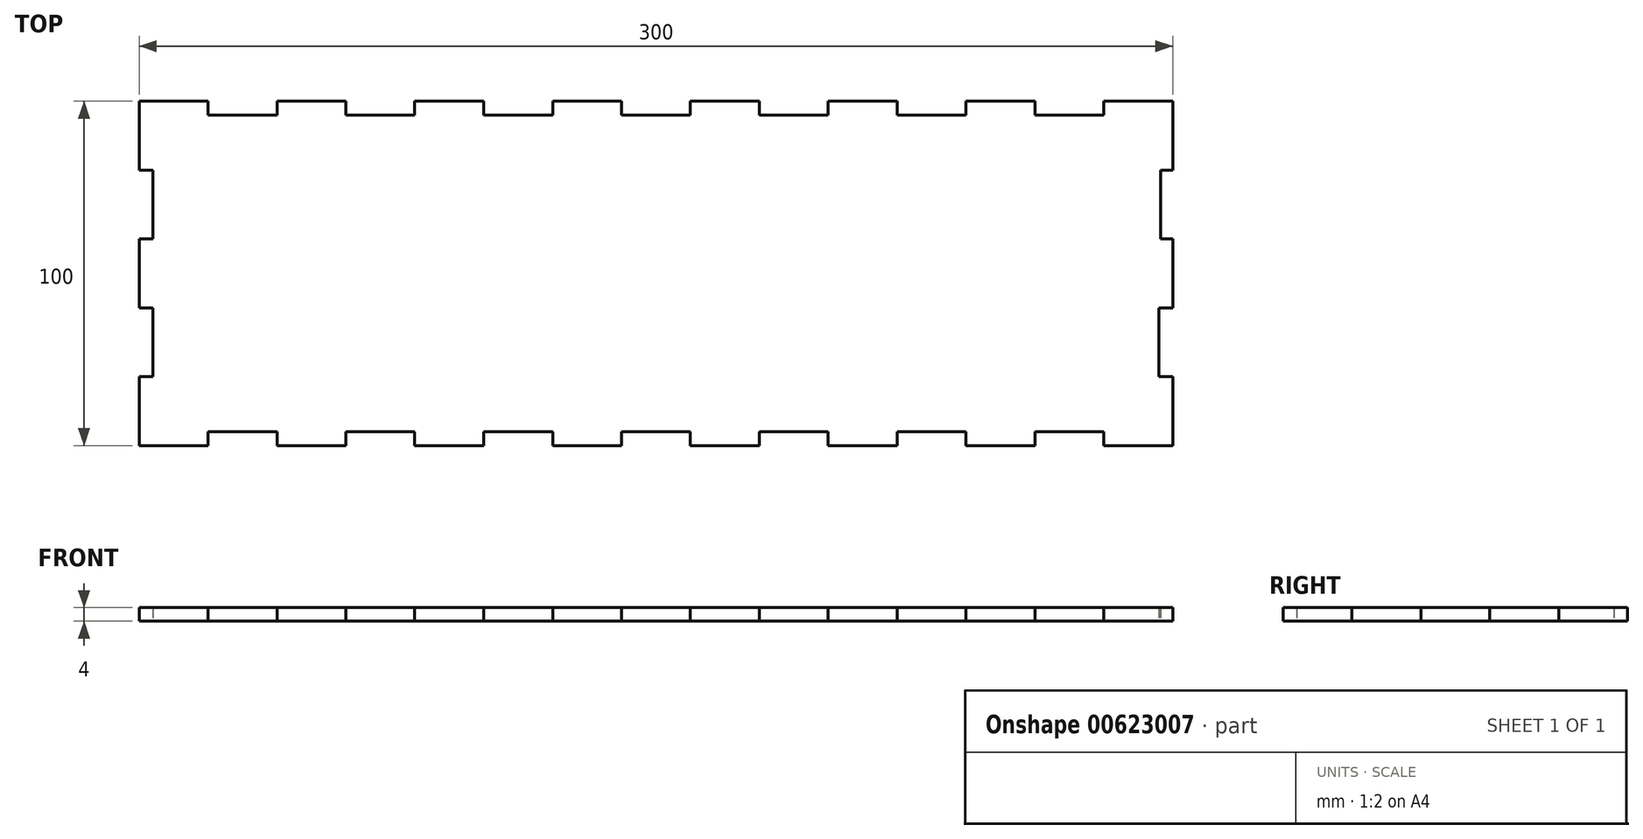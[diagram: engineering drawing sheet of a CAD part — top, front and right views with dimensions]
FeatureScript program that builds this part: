
annotation { "Feature Type Name" : "Feature", "Feature Type Description" : "" }
export const myFeature = defineFeature(function(context is Context, id is Id, definition is map)
    precondition{}
    {
        {
            var Q0;
            Q0=qCreatedBy(makeId("Top.planeOp"),FACE);
            var sketch = newSketch(context, id + "F0", { "sketchPlane" : qUnion([Q0])});
            skLineSegment(sketch, "E0.bottom", {"start": v(0, 0) * mm, "end": v(-300, 0) * mm});
            skLineSegment(sketch, "E0.top", {"start": v(0, 100) * mm, "end": v(-300, 100) * mm});
            skLineSegment(sketch, "E0.left", {"start": v(0, 0) * mm, "end": v(0, 100) * mm});
            skLineSegment(sketch, "E0.right", {"start": v(-300, 0) * mm, "end": v(-300, 100) * mm});
            skLineSegment(sketch, "E1.bottom", {"start": v(-280, 0) * mm, "end": v(-260, 0) * mm});
            skLineSegment(sketch, "E1.top", {"start": v(-280, 4) * mm, "end": v(-260, 4) * mm});
            skLineSegment(sketch, "E1.left", {"start": v(-280, 0) * mm, "end": v(-280, 4) * mm});
            skLineSegment(sketch, "E1.right", {"start": v(-260, 0) * mm, "end": v(-260, 4) * mm});
            skLineSegment(sketch, "E2.bottom", {"start": v(-240, 0) * mm, "end": v(-220, 0) * mm});
            skLineSegment(sketch, "E2.top", {"start": v(-240, 4) * mm, "end": v(-220, 4) * mm});
            skLineSegment(sketch, "E2.left", {"start": v(-240, 0) * mm, "end": v(-240, 4) * mm});
            skLineSegment(sketch, "E2.right", {"start": v(-220, 0) * mm, "end": v(-220, 4) * mm});
            skLineSegment(sketch, "E3.bottom", {"start": v(-200, 0) * mm, "end": v(-180, 0) * mm});
            skLineSegment(sketch, "E3.top", {"start": v(-200, 4) * mm, "end": v(-180, 4) * mm});
            skLineSegment(sketch, "E3.left", {"start": v(-200, 0) * mm, "end": v(-200, 4) * mm});
            skLineSegment(sketch, "E3.right", {"start": v(-180, 0) * mm, "end": v(-180, 4) * mm});
            skLineSegment(sketch, "E4.bottom", {"start": v(-160, 0) * mm, "end": v(-140, 0) * mm});
            skLineSegment(sketch, "E4.top", {"start": v(-160, 4) * mm, "end": v(-140, 4) * mm});
            skLineSegment(sketch, "E4.left", {"start": v(-160, 0) * mm, "end": v(-160, 4) * mm});
            skLineSegment(sketch, "E4.right", {"start": v(-140, 0) * mm, "end": v(-140, 4) * mm});
            skLineSegment(sketch, "E5.bottom", {"start": v(-120, 0) * mm, "end": v(-100, 0) * mm});
            skLineSegment(sketch, "E5.top", {"start": v(-120, 4) * mm, "end": v(-100, 4) * mm});
            skLineSegment(sketch, "E5.left", {"start": v(-120, 0) * mm, "end": v(-120, 4) * mm});
            skLineSegment(sketch, "E5.right", {"start": v(-100, 0) * mm, "end": v(-100, 4) * mm});
            skLineSegment(sketch, "E6.bottom", {"start": v(-80, 0) * mm, "end": v(-60, 0) * mm});
            skLineSegment(sketch, "E6.top", {"start": v(-80, 4) * mm, "end": v(-60, 4) * mm});
            skLineSegment(sketch, "E6.left", {"start": v(-80, 0) * mm, "end": v(-80, 4) * mm});
            skLineSegment(sketch, "E6.right", {"start": v(-60, 0) * mm, "end": v(-60, 4) * mm});
            skLineSegment(sketch, "E7.bottom", {"start": v(-40, 0) * mm, "end": v(-20, 0) * mm});
            skLineSegment(sketch, "E7.top", {"start": v(-40, 4) * mm, "end": v(-20, 4) * mm});
            skLineSegment(sketch, "E7.left", {"start": v(-40, 0) * mm, "end": v(-40, 4) * mm});
            skLineSegment(sketch, "E7.right", {"start": v(-20, 0) * mm, "end": v(-20, 4) * mm});
            skLineSegment(sketch, "E8.bottom", {"start": v(-280, 100) * mm, "end": v(-260, 100) * mm});
            skLineSegment(sketch, "E8.top", {"start": v(-280, 96) * mm, "end": v(-260, 96) * mm});
            skLineSegment(sketch, "E8.left", {"start": v(-280, 100) * mm, "end": v(-280, 96) * mm});
            skLineSegment(sketch, "E8.right", {"start": v(-260, 100) * mm, "end": v(-260, 96) * mm});
            skLineSegment(sketch, "E9.bottom", {"start": v(-240, 100) * mm, "end": v(-220, 100) * mm});
            skLineSegment(sketch, "E9.top", {"start": v(-240, 96) * mm, "end": v(-220, 96) * mm});
            skLineSegment(sketch, "E9.left", {"start": v(-240, 100) * mm, "end": v(-240, 96) * mm});
            skLineSegment(sketch, "E9.right", {"start": v(-220, 100) * mm, "end": v(-220, 96) * mm});
            skLineSegment(sketch, "E10.bottom", {"start": v(-200, 100) * mm, "end": v(-180, 100) * mm});
            skLineSegment(sketch, "E10.top", {"start": v(-200, 96) * mm, "end": v(-180, 96) * mm});
            skLineSegment(sketch, "E10.left", {"start": v(-200, 100) * mm, "end": v(-200, 96) * mm});
            skLineSegment(sketch, "E10.right", {"start": v(-180, 100) * mm, "end": v(-180, 96) * mm});
            skLineSegment(sketch, "E11.bottom", {"start": v(-160, 100) * mm, "end": v(-140, 100) * mm});
            skLineSegment(sketch, "E11.top", {"start": v(-160, 96) * mm, "end": v(-140, 96) * mm});
            skLineSegment(sketch, "E11.left", {"start": v(-160, 100) * mm, "end": v(-160, 96) * mm});
            skLineSegment(sketch, "E11.right", {"start": v(-140, 100) * mm, "end": v(-140, 96) * mm});
            skLineSegment(sketch, "E12.bottom", {"start": v(-120, 100) * mm, "end": v(-100, 100) * mm});
            skLineSegment(sketch, "E12.top", {"start": v(-120, 96) * mm, "end": v(-100, 96) * mm});
            skLineSegment(sketch, "E12.left", {"start": v(-120, 100) * mm, "end": v(-120, 96) * mm});
            skLineSegment(sketch, "E12.right", {"start": v(-100, 100) * mm, "end": v(-100, 96) * mm});
            skLineSegment(sketch, "E13.bottom", {"start": v(-80, 100) * mm, "end": v(-60, 100) * mm});
            skLineSegment(sketch, "E13.top", {"start": v(-80, 96) * mm, "end": v(-60, 96) * mm});
            skLineSegment(sketch, "E13.left", {"start": v(-80, 100) * mm, "end": v(-80, 96) * mm});
            skLineSegment(sketch, "E13.right", {"start": v(-60, 100) * mm, "end": v(-60, 96) * mm});
            skPoint(sketch, "E14.oppositeSnap0", {"position": v(-70, 96) * mm});
            skLineSegment(sketch, "E14.bottom", {"start": v(-40, 100) * mm, "end": v(-20, 100) * mm});
            skLineSegment(sketch, "E14.top", {"start": v(-40, 96) * mm, "end": v(-20, 96) * mm});
            skLineSegment(sketch, "E14.left", {"start": v(-40, 100) * mm, "end": v(-40, 96) * mm});
            skLineSegment(sketch, "E14.right", {"start": v(-20, 100) * mm, "end": v(-20, 96) * mm});
            skLineSegment(sketch, "E15.bottom", {"start": v(0, 60) * mm, "end": v(-3.56, 60) * mm});
            skLineSegment(sketch, "E15.top", {"start": v(0, 80) * mm, "end": v(-3.56, 80) * mm});
            skLineSegment(sketch, "E15.left", {"start": v(0, 80) * mm, "end": v(0, 60) * mm});
            skLineSegment(sketch, "E15.right", {"start": v(-3.56, 80) * mm, "end": v(-3.56, 60) * mm});
            skLineSegment(sketch, "E16.bottom", {"start": v(0, 20) * mm, "end": v(-4, 20) * mm});
            skLineSegment(sketch, "E16.top", {"start": v(0, 40) * mm, "end": v(-4, 40) * mm});
            skLineSegment(sketch, "E16.left", {"start": v(0, 20) * mm, "end": v(0, 40) * mm});
            skLineSegment(sketch, "E16.right", {"start": v(-4, 20) * mm, "end": v(-4, 40) * mm});
            skLineSegment(sketch, "E17.bottom", {"start": v(-300, 80) * mm, "end": v(-296, 80) * mm});
            skLineSegment(sketch, "E17.top", {"start": v(-300, 60) * mm, "end": v(-296, 60) * mm});
            skLineSegment(sketch, "E17.left", {"start": v(-300, 80) * mm, "end": v(-300, 60) * mm});
            skLineSegment(sketch, "E17.right", {"start": v(-296, 80) * mm, "end": v(-296, 60) * mm});
            skLineSegment(sketch, "E18.bottom", {"start": v(-300, 40) * mm, "end": v(-296, 40) * mm});
            skLineSegment(sketch, "E18.top", {"start": v(-300, 20) * mm, "end": v(-296, 20) * mm});
            skLineSegment(sketch, "E18.left", {"start": v(-300, 40) * mm, "end": v(-300, 20) * mm});
            skLineSegment(sketch, "E18.right", {"start": v(-296, 40) * mm, "end": v(-296, 20) * mm});
            skSolve(sketch);
        }
        {
            var Q0;
            Q0=makeQuery(id+"F0.imprint","IMPRINT",FACE,{"disambiguationData":[TD([[makeQuery(id+"F0.imprint","IMPRINT",EDGE,{"derivedFrom":sQuery(id+"F0.wireOp",EDGE,"E1.top")}),1.0]])]});
            extrude(context, id + "F1", {"entities" : qUnion([Q0]), "depth" : 4 * mm, "offsetDistance" : 25 * mm});
        }
    });
